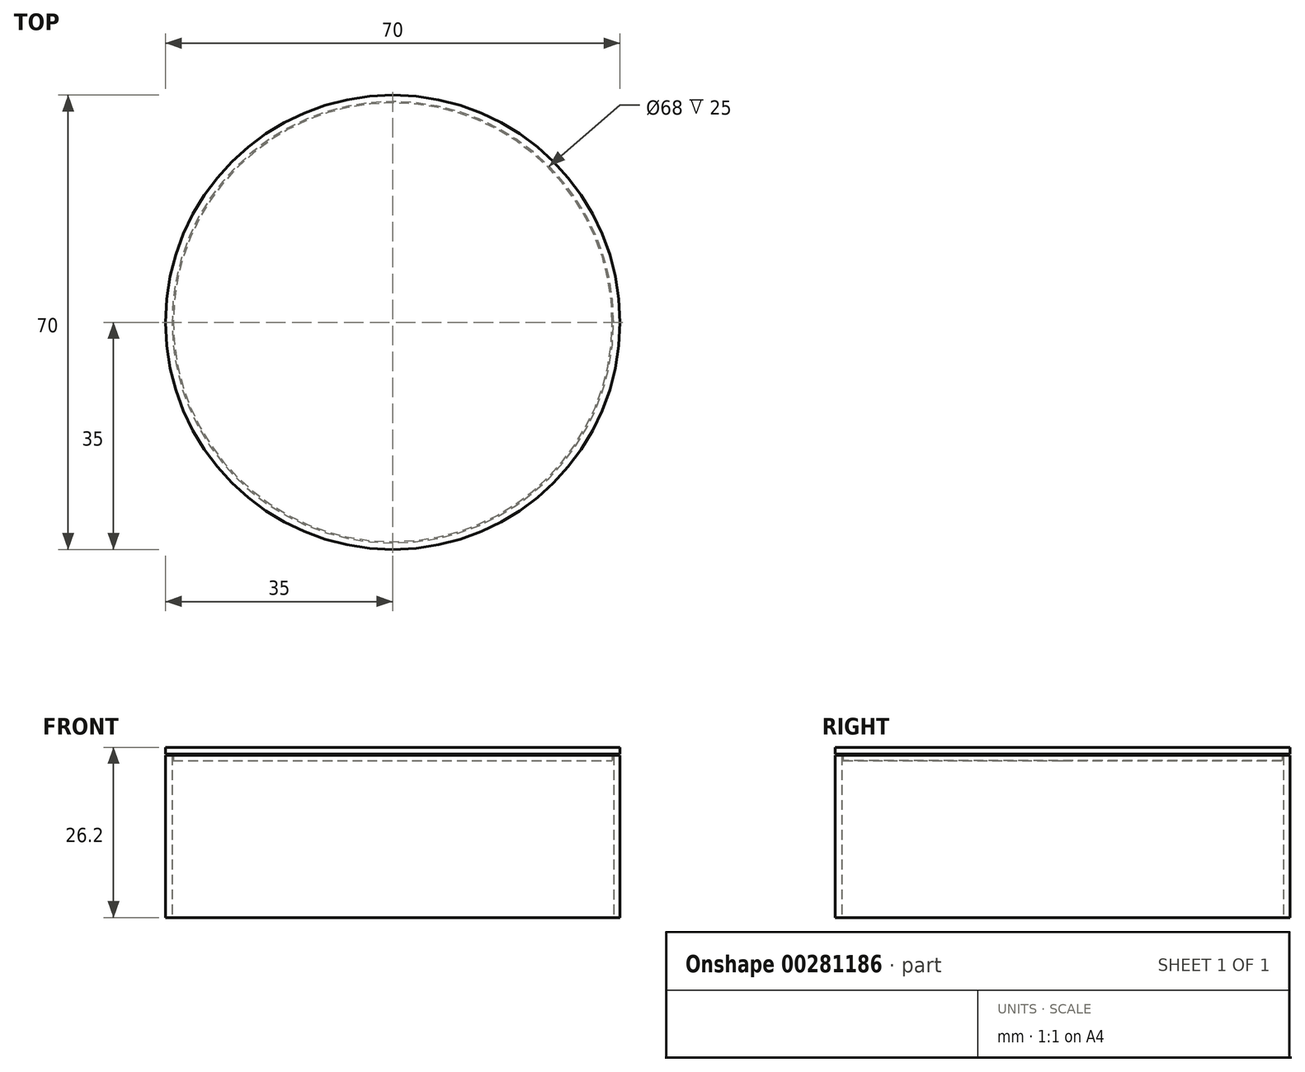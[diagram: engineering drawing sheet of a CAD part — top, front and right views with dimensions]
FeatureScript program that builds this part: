
annotation { "Feature Type Name" : "Feature", "Feature Type Description" : "" }
export const myFeature = defineFeature(function(context is Context, id is Id, definition is map)
    precondition{}
    {
        {
            var Q0;
            Q0=qCreatedBy(makeId("Top.planeOp"),FACE);
            var sketch = newSketch(context, id + "F0", { "sketchPlane" : qUnion([Q0])});
            skCircle(sketch, "E0", {"center": v(0, 0) * mm, "radius": 35 * mm});
            skCircle(sketch, "E1", {"center": v(0, 0) * mm, "radius": 34 * mm});
            skSolve(sketch);
        }
        {
            var Q0;
            Q0 = qSketchRegion(id + "F0", true);
            extrude(context, id + "F1", {"entities" : qUnion([Q0]), "depth" : 25 * mm});
        }
        {
            var Q0;
            Q0=qCreatedBy(makeId("Front.planeOp"),FACE);
            var sketch = newSketch(context, id + "F2", { "sketchPlane" : qUnion([Q0])});
            skLineSegment(sketch, "E2", {"start": v(-35, 25.2) * mm, "end": v(-33.8, 25.2) * mm});
            skLineSegment(sketch, "E3", {"start": v(-33.8, 25.2) * mm, "end": v(-33.8, 24.2) * mm});
            skLineSegment(sketch, "E4", {"start": v(-33.8, 24.2) * mm, "end": v(0, 24.2) * mm});
            skLineSegment(sketch, "E5", {"start": v(0, 24.2) * mm, "end": v(0, 26.2) * mm});
            skLineSegment(sketch, "E6", {"start": v(0, 26.2) * mm, "end": v(-35, 26.2) * mm});
            skLineSegment(sketch, "E7", {"start": v(-35, 26.2) * mm, "end": v(-35, 25.2) * mm});
            skSolve(sketch);
        }
        {
            var Q0;
            Q0 = qSketchRegion(id + "F2", true);
            var Q1;
            Q1 = qConstructionFilter(qBodyType(qCreatedBy(id + "F2" ,EDGE), BodyType.WIRE), ConstructionObject.NO);
            var Q2;
            Q2=sQuery(id+"F2.wireOp",EDGE,"E5");
            revolve(context, id + "F3", {"entities" : qUnion([Q0]), "surfaceEntities" : qUnion([Q1]), "axis" : qUnion([Q2]), "revolveType" : RevolveType.FULL});
        }
    });
